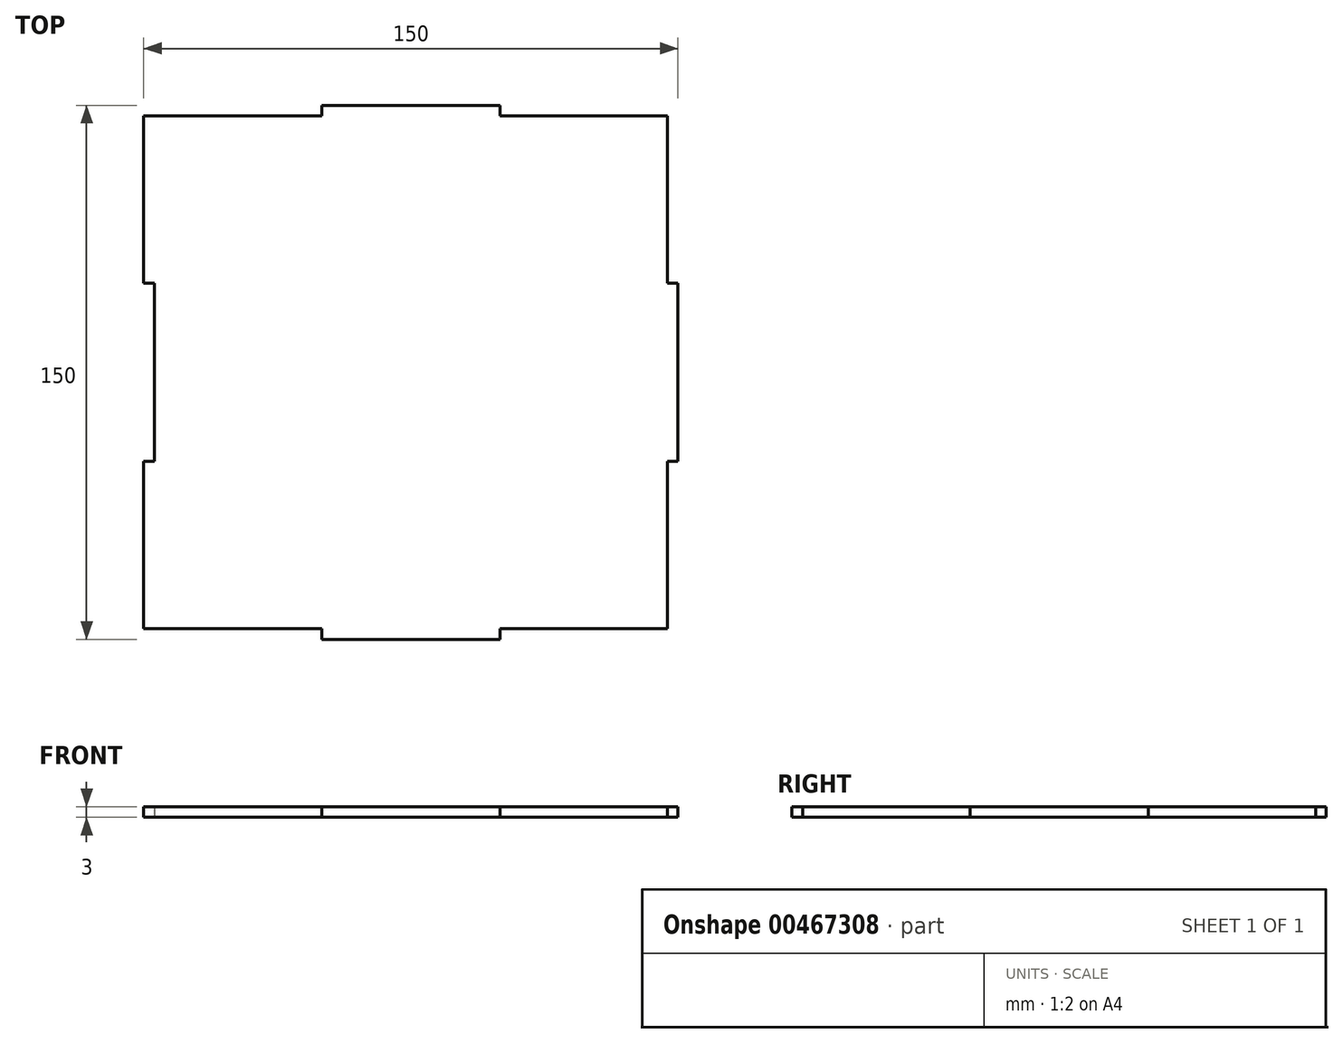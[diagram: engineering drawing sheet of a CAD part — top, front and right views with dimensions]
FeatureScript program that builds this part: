
annotation { "Feature Type Name" : "Feature", "Feature Type Description" : "" }
export const myFeature = defineFeature(function(context is Context, id is Id, definition is map)
    precondition{}
    {
        {
            var Q0;
            Q0=qCreatedBy(makeId("Top.planeOp"),FACE);
            var sketch = newSketch(context, id + "F0", { "sketchPlane" : qUnion([Q0])});
            skLineSegment(sketch, "E0.bottom", {"start": v(25, 75) * mm, "end": v(-25, 75) * mm});
            skLineSegment(sketch, "E0.top", {"start": v(25, -75) * mm, "end": v(-25, -75) * mm});
            skLineSegment(sketch, "E0.left", {"start": v(75, 25) * mm, "end": v(75, -25) * mm});
            skLineSegment(sketch, "E0.right", {"start": v(-75, 72) * mm, "end": v(-75, 25) * mm});
            skPoint(sketch, "E0.middle", {"position": v(0, 0) * mm});
            skLineSegment(sketch, "E1", {"start": v(-75, 72) * mm, "end": v(-25, 72) * mm});
            skLineSegment(sketch, "E2", {"start": v(-25, 72) * mm, "end": v(-25, 75) * mm});
            skLineSegment(sketch, "E3", {"start": v(72, 72) * mm, "end": v(25, 72) * mm});
            skLineSegment(sketch, "E4", {"start": v(25, 72) * mm, "end": v(25, 75) * mm});
            skPoint(sketch, "E5.orphan", {"position": v(-75, 75) * mm});
            skPoint(sketch, "E6.orphan", {"position": v(75, 75) * mm});
            skLineSegment(sketch, "E7", {"start": v(-75, -72) * mm, "end": v(-25, -72) * mm});
            skLineSegment(sketch, "E8", {"start": v(-25, -72) * mm, "end": v(-25, -75) * mm});
            skLineSegment(sketch, "E9", {"start": v(72, -72) * mm, "end": v(25, -72) * mm});
            skLineSegment(sketch, "E10", {"start": v(25, -72) * mm, "end": v(25, -75) * mm});
            skPoint(sketch, "E11.orphan", {"position": v(-75, -75) * mm});
            skPoint(sketch, "E12.orphan", {"position": v(75, -75) * mm});
            skLineSegment(sketch, "E13", {"start": v(-75, 25) * mm, "end": v(-72, 25) * mm});
            skLineSegment(sketch, "E14", {"start": v(-72, 25) * mm, "end": v(-72, -25) * mm});
            skLineSegment(sketch, "E15", {"start": v(-72, -25) * mm, "end": v(-75, -25) * mm});
            skLineSegment(sketch, "E16.trimOffspring", {"start": v(-75, -25) * mm, "end": v(-75, -72) * mm});
            skLineSegment(sketch, "E17", {"start": v(72, 72) * mm, "end": v(72, 25) * mm});
            skLineSegment(sketch, "E18", {"start": v(72, 25) * mm, "end": v(75, 25) * mm});
            skLineSegment(sketch, "E19", {"start": v(72, -72) * mm, "end": v(72, -25) * mm});
            skLineSegment(sketch, "E20", {"start": v(72, -25) * mm, "end": v(75, -25) * mm});
            skPoint(sketch, "E21.start.orphan", {"position": v(75, 72) * mm});
            skSolve(sketch);
        }
        {
            var Q0;
            Q0=makeQuery(id+"F0.imprint","IMPRINT",FACE,{"disambiguationData":[TD([[makeQuery(id+"F0.imprint","IMPRINT",EDGE,{"derivedFrom":sQuery(id+"F0.wireOp",EDGE,"E0.bottom")}),1.0]])]});
            extrude(context, id + "F1", {"entities" : qUnion([Q0]), "depth" : 3 * mm});
        }
    });
